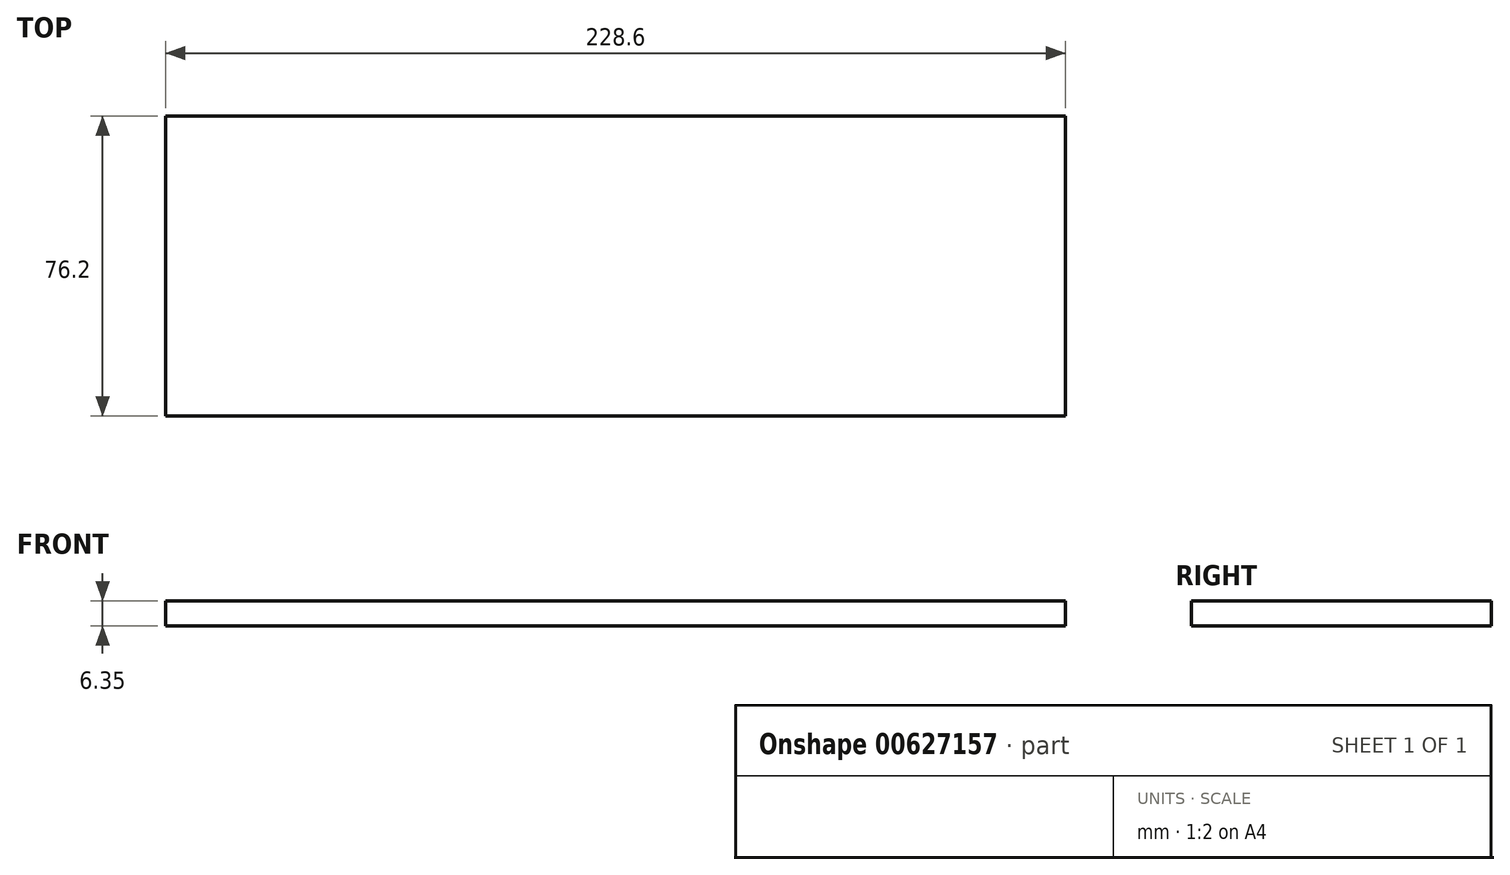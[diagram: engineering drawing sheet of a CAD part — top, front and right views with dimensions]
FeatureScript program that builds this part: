
annotation { "Feature Type Name" : "Feature", "Feature Type Description" : "" }
export const myFeature = defineFeature(function(context is Context, id is Id, definition is map)
    precondition{}
    {
        {
            var Q0;
            Q0=qCreatedBy(makeId("Top.planeOp"),FACE);
            var sketch = newSketch(context, id + "F0", { "sketchPlane" : qUnion([Q0])});
            skLineSegment(sketch, "E0.bottom", {"start": v(0, 0) * mm, "end": v(-228.6, 0) * mm});
            skLineSegment(sketch, "E0.top", {"start": v(0, 76.2) * mm, "end": v(-228.6, 76.2) * mm});
            skLineSegment(sketch, "E0.left", {"start": v(0, 0) * mm, "end": v(0, 76.2) * mm});
            skLineSegment(sketch, "E0.right", {"start": v(-228.6, 0) * mm, "end": v(-228.6, 76.2) * mm});
            skSolve(sketch);
        }
        {
            var Q0;
            Q0=makeQuery(id+"F0.imprint","IMPRINT",FACE,{"disambiguationData":[TD([[makeQuery(id+"F0.imprint","IMPRINT",EDGE,{"derivedFrom":sQuery(id+"F0.wireOp",EDGE,"E0.bottom")}),-1.0]])]});
            extrude(context, id + "F1", {"entities" : qUnion([Q0]), "depth" : 6.35 * mm, "offsetDistance" : 25 * mm});
        }
    });
